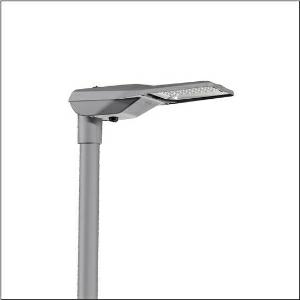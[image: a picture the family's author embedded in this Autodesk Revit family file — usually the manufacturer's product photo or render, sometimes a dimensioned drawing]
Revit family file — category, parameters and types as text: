
# Revit family: streetlight_sl_21_iq_mini___st1_0a_5xe2d21y08gb_b3c5
name_source: partatom
category: Lighting Fixtures
units: mm (PartAtom-declared; Revit-internal decimal feet)

## family parameters
Cut with Voids When Loaded = No
Host = Face
Light Source = No
Part Type = Normal
Room Calculation Point = No
Round Connector Dimension = Use Diameter
Shared = No

## types (1)
- --- (1 x LED, 4810 lm, 39.8 W, 2200K)
    Apparent Load = 40 VA
    CIE Flux Codes = 37 72 97 100 100
    Color Rendering = 70
    Color Temperature = 2200K
    Default Elevation = 1800 mm
    Description = Streetlight SL 21 iQ mini, mast luminaire, primary light control with lens, of PMMA, primary optical cover: cover, of toughened safety glass, transparent, light distribution: ST1.0a, light emission: direct distribution, primary light characteristic: asymmetric, installation type: post-top, side-entry, LED, High Power LED, rated luminous flux: 4.810lm, luminous efficacy: 121lm/W, light colour: 722, colour temperature: 2200K, control gear: iQ-Street Remote, D4i with power reduction, control: pre-setting: logarithmic dimming characteristic, Street-Remote, Auto-Match, Temp-Guard, Lumen-Switch, Night-Set, Smart-Wire, Light-Fading, Desk-Remote (wireless, voltage-free reading and setting of iQ features in the workshop via application-optimized NFC function/RFID function), optimised constant luminous flux control (CLO 2.0), mains connection: 220..240V, AC, 50/60Hz, start of lifetime: 40W, end of service life: 41W, reduction: 18W, luminaire housing, of diecast aluminium, powder-coated, Siteco® metallic grey (DB 702S), corrosivity category C5 mid according to DIN EN ISO 12944, please order mast flange separately, inclination adjustable: 0°, 5°, 10°, 15°, sealing non-destructively replaceable, multi-level sealing system, length: 628mm, width: 235mm, height: 110mm, mast flange for spigot size: 42mm (side-entry): 5XC10008XM4, 60/48mm (side-entry/post-top): 5XC10108XM2, 76/60mm (side-entry/post-top): 5XC10108XM1, mounting height: 4..8m, Smart Interface below and above, protection rating (complete): IP66, insulation class (complete): insulation class II (safety insulation), certification: CE, ENEC, ENEC+, VDE, impact resistance: IK10, permissible operating ambient temperature for outdoor applications: -40..+50°C, standard-compliant lighting for roads and squares, packaging unit: 1 piece

Light Distribution: ST1.0a
    Height = 110 mm
    Lamp = 1 x LED
    Lamp Light Flux = 4810 lm
    Lamp Power = 39.8 W
    Lamp count = 1
    Length = 625 mm
    Luminous efficacy = 121 lm/W
    Manufacturer = Siteco
    ModVariant = No
    Model = 5XE2D21Y08GB
    Number of Poles = 1
    OnlyDefault = Yes
    Power Factor = 1
    Product Name = Streetlight SL 21 iQ mini | ST1.0a
    Product group = mast luminaire | pylon top
    ProductGroupID = 6100
    Protection Class = Protection class II
    Protection Degree = IP 66
    RLX_Detail_Level = 1
    RLX_Emergency_Light_Flux = 0 lm
    RLX_Emergency_Type = 0
    RLX_Emergency_Type_DB = No
    RlxData = <blob elided: 26813 chars, md5=9cdf7a4f>
    Socket = socket
    Standby Power = 0 W
    System Light Flux = 4810 lm
    System Power = 40 W
    Type Comments = factory setting: luminous flux: 100 % | dim-lin: 254 | 800 mA
    Type Image = l_1003514.jpg
    URL = http://relux.com
    VarID = @adj_115070
    Voltage = 0 V
    Weight = 0.00 kg
    Width = 234 mm

## geometry (parser evidence)
native form markers: Blend x4, Sweep x12
no freeform markers — native parametric forms only
